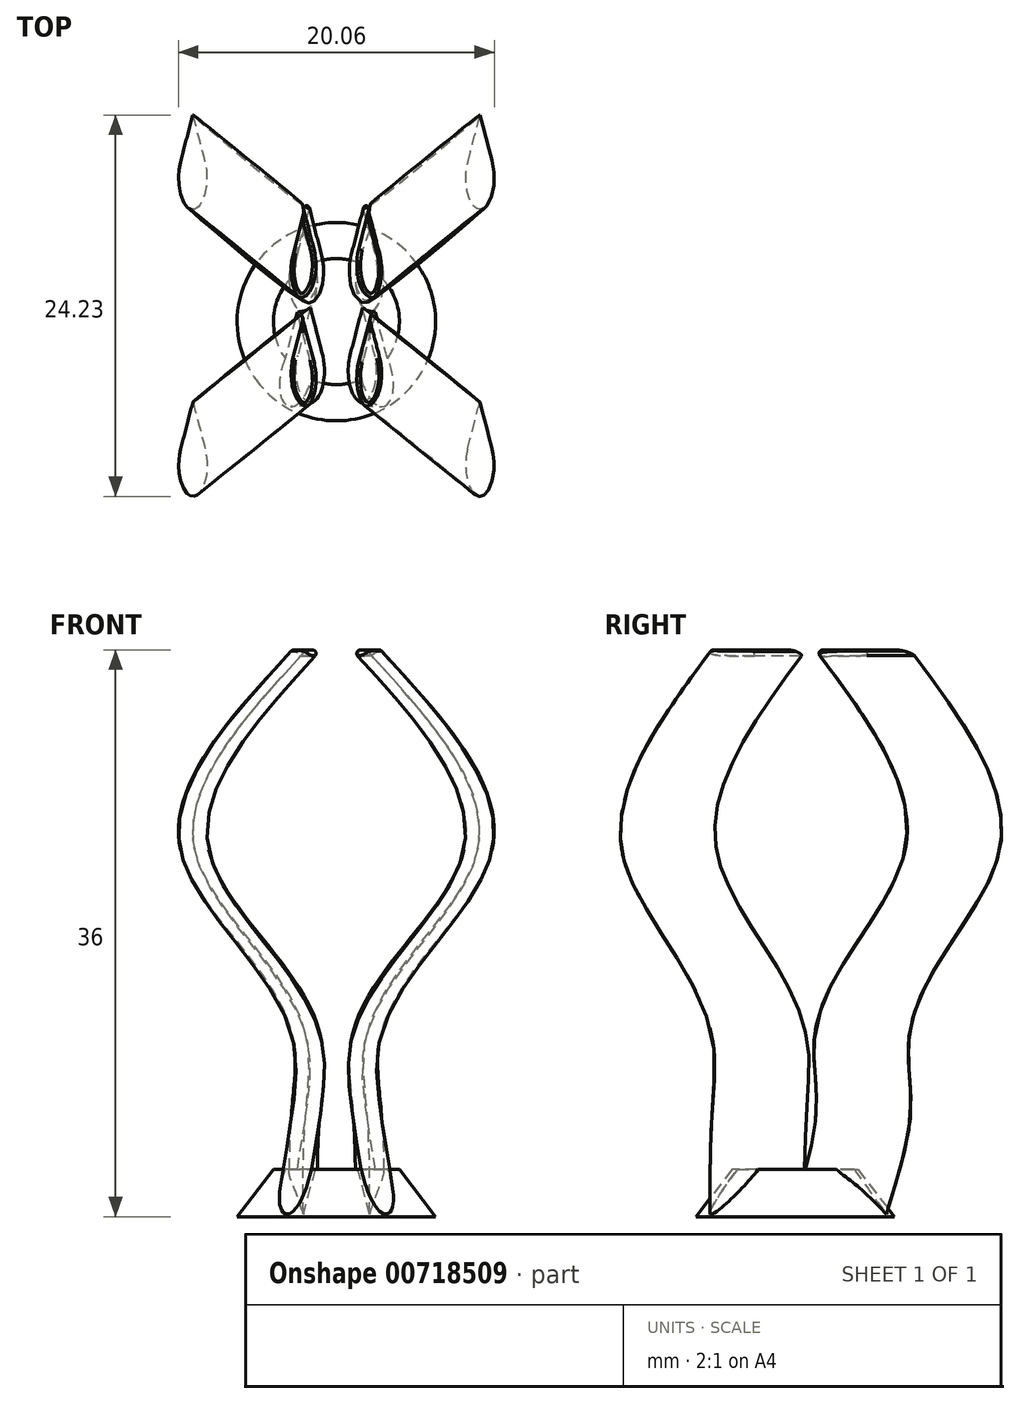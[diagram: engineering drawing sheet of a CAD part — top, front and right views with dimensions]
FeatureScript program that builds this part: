
annotation { "Feature Type Name" : "Feature", "Feature Type Description" : "" }
export const myFeature = defineFeature(function(context is Context, id is Id, definition is map)
    precondition{}
    {
        {
            var Q0;
            Q0=qCreatedBy(makeId("Top.planeOp"),FACE);
            var sketch = newSketch(context, id + "F0", { "sketchPlane" : qUnion([Q0])});
            skCircle(sketch, "E0", {"center": v(0, 0) * mm, "radius": 6.3 * mm});
            skSolve(sketch);
        }
        {
            assignVariable(context, id + "F1", {"variableType" : VariableType.LENGTH, "name" : "BaseHeight", "lengthValue" : 3 * mm});
        }
        {
            var Q0;
            Q0=qCreatedBy(makeId("Top.planeOp"),FACE);
            cPlane(context, id + "F2", {"entities" : qUnion([Q0]), "cplaneType" : CPlaneType.OFFSET, "offset" : getVariable(context, 'BaseHeight'), "width" : 150 * mm, "height" : 150 * mm});
        }
        {
            var Q0;
            Q0=qCreatedBy(id+"F2.planeOp",FACE);
            var sketch = newSketch(context, id + "F3", { "sketchPlane" : qUnion([Q0])});
            skCircle(sketch, "E1", {"center": v(0, 0) * mm, "radius": 4 * mm});
            skSolve(sketch);
        }
        {
            assignVariable(context, id + "F4", {"variableType" : VariableType.LENGTH, "name" : "PostH1", "lengthValue" : 6 * mm});
        }
        {
            assignVariable(context, id + "F5", {"variableType" : VariableType.LENGTH, "name" : "PostH2", "lengthValue" : 11 * mm});
        }
        {
            assignVariable(context, id + "F6", {"variableType" : VariableType.LENGTH, "name" : "PostH3", "lengthValue" : 23.3 * mm});
        }
        {
            assignVariable(context, id + "F7", {"variableType" : VariableType.LENGTH, "name" : "PostH4", "lengthValue" : 36 * mm});
        }
        {
            var Q0;
            Q0=qCreatedBy(makeId("Top.planeOp"),FACE);
            cPlane(context, id + "F8", {"entities" : qUnion([Q0]), "cplaneType" : CPlaneType.OFFSET, "offset" : getVariable(context, 'PostH1'), "width" : 150 * mm, "height" : 150 * mm});
        }
        {
            var Q0;
            Q0=qCreatedBy(makeId("Top.planeOp"),FACE);
            cPlane(context, id + "F9", {"entities" : qUnion([Q0]), "cplaneType" : CPlaneType.OFFSET, "offset" : getVariable(context, 'PostH2'), "width" : 150 * mm, "height" : 150 * mm});
        }
        {
            var Q0;
            Q0=qCreatedBy(makeId("Top.planeOp"),FACE);
            cPlane(context, id + "F10", {"entities" : qUnion([Q0]), "cplaneType" : CPlaneType.OFFSET, "offset" : getVariable(context, 'PostH3'), "width" : 150 * mm, "height" : 150 * mm});
        }
        {
            var Q0;
            Q0=qCreatedBy(makeId("Top.planeOp"),FACE);
            cPlane(context, id + "F11", {"entities" : qUnion([Q0]), "cplaneType" : CPlaneType.OFFSET, "offset" : getVariable(context, 'PostH4'), "width" : 150 * mm, "height" : 150 * mm});
        }
        {
            var Q0;
            Q0=makeQuery(id+"F0.imprint","IMPRINT",FACE,{"disambiguationData":[TD([[makeQuery(id+"F0.imprint","IMPRINT",EDGE,{"derivedFrom":sQuery(id+"F0.wireOp",EDGE,"E0")}),1.0]])]});
            var Q1;
            Q1=makeQuery(id+"F3.imprint","IMPRINT",FACE,{"disambiguationData":[TD([[makeQuery(id+"F3.imprint","IMPRINT",EDGE,{"derivedFrom":sQuery(id+"F3.wireOp",EDGE,"E1")}),1.0]])]});
            loft(context, id + "F12", {"sheetProfilesArray" : [{ "sheetProfileEntities" : qUnion([Q0]) }, { "sheetProfileEntities" : qUnion([Q1]) }]});
        }
        {
            var Q0;
            Q0=qCreatedBy(makeId("Top.planeOp"),FACE);
            var sketch = newSketch(context, id + "F13", { "sketchPlane" : qUnion([Q0])});
            skEllipse(sketch, "E2", {"center": v(-2.1, 1.8) * mm, "majorRadius": 2 * mm, "minorRadius": 0.9 * mm, "majorAxis": v(0, 1)});
            skLineSegment(sketch, "E3", {"start": v(-2.88, 2.8) * mm, "end": v(-2.1, 5.8) * mm});
            skLineSegment(sketch, "E4", {"start": v(-2.1, 5.8) * mm, "end": v(-1.32, 2.8) * mm});
            skEllipse(sketch, "E5", {"center": v(2.1, 1.8) * mm, "majorRadius": 2 * mm, "minorRadius": 0.9 * mm, "majorAxis": v(0, 1)});
            skLineSegment(sketch, "E6", {"start": v(1.32, 2.8) * mm, "end": v(2.1, 5.8) * mm});
            skLineSegment(sketch, "E7", {"start": v(2.1, 5.8) * mm, "end": v(2.88, 2.8) * mm});
            skEllipse(sketch, "E8", {"center": v(-2.9, -3.4) * mm, "majorRadius": 2 * mm, "minorRadius": 0.9 * mm, "majorAxis": v(0, 1)});
            skLineSegment(sketch, "E9", {"start": v(-3.68, -2.4) * mm, "end": v(-2.9, 0.6) * mm});
            skLineSegment(sketch, "E10", {"start": v(-2.9, 0.6) * mm, "end": v(-2.12, -2.4) * mm});
            skEllipse(sketch, "E11", {"center": v(2.9, -3.4) * mm, "majorRadius": 2 * mm, "minorRadius": 0.9 * mm, "majorAxis": v(0, 1)});
            skLineSegment(sketch, "E12", {"start": v(2.12, -2.4) * mm, "end": v(2.9, 0.6) * mm});
            skLineSegment(sketch, "E13", {"start": v(2.9, 0.6) * mm, "end": v(3.68, -2.4) * mm});
            skSolve(sketch);
        }
        {
            var Q0;
            Q0=qCreatedBy(id+"F8.planeOp",FACE);
            var sketch = newSketch(context, id + "F14", { "sketchPlane" : qUnion([Q0])});
            skEllipse(sketch, "E14", {"center": v(-2, 3.3) * mm, "majorRadius": 2 * mm, "minorRadius": 0.9 * mm, "majorAxis": v(0, 1)});
            skLineSegment(sketch, "E15", {"start": v(-2.78, 4.3) * mm, "end": v(-2, 7.3) * mm});
            skLineSegment(sketch, "E16", {"start": v(-2, 7.3) * mm, "end": v(-1.22, 4.3) * mm});
            skEllipse(sketch, "E17", {"center": v(2, 3.3) * mm, "majorRadius": 2 * mm, "minorRadius": 0.9 * mm, "majorAxis": v(0, 1)});
            skLineSegment(sketch, "E18", {"start": v(1.22, 4.3) * mm, "end": v(2, 7.3) * mm});
            skLineSegment(sketch, "E19", {"start": v(2, 7.3) * mm, "end": v(2.78, 4.3) * mm});
            skEllipse(sketch, "E20", {"center": v(-2, -3.3) * mm, "majorRadius": 2 * mm, "minorRadius": 0.9 * mm, "majorAxis": v(0, 1)});
            skLineSegment(sketch, "E21", {"start": v(-2.78, -2.3) * mm, "end": v(-2, 0.7) * mm});
            skLineSegment(sketch, "E22", {"start": v(-2, 0.7) * mm, "end": v(-1.22, -2.3) * mm});
            skEllipse(sketch, "E23", {"center": v(2, -3.3) * mm, "majorRadius": 2 * mm, "minorRadius": 0.9 * mm, "majorAxis": v(0, 1)});
            skLineSegment(sketch, "E24", {"start": v(1.22, -2.3) * mm, "end": v(2, 0.7) * mm});
            skLineSegment(sketch, "E25", {"start": v(2, 0.7) * mm, "end": v(2.78, -2.3) * mm});
            skSolve(sketch);
        }
        {
            var Q0;
            Q0=qCreatedBy(id+"F9.planeOp",FACE);
            var sketch = newSketch(context, id + "F15", { "sketchPlane" : qUnion([Q0])});
            skEllipse(sketch, "E26", {"center": v(-1.8, 3.2) * mm, "majorRadius": 2 * mm, "minorRadius": 0.9 * mm, "majorAxis": v(0, 1)});
            skLineSegment(sketch, "E27", {"start": v(-2.58, 4.2) * mm, "end": v(-1.8, 7.2) * mm});
            skLineSegment(sketch, "E28", {"start": v(-1.8, 7.2) * mm, "end": v(-1.02, 4.2) * mm});
            skEllipse(sketch, "E29", {"center": v(1.8, 3.2) * mm, "majorRadius": 2 * mm, "minorRadius": 0.9 * mm, "majorAxis": v(0, 1)});
            skLineSegment(sketch, "E30", {"start": v(1.02, 4.2) * mm, "end": v(1.8, 7.2) * mm});
            skLineSegment(sketch, "E31", {"start": v(1.8, 7.2) * mm, "end": v(2.58, 4.2) * mm});
            skEllipse(sketch, "E32", {"center": v(-1.8, -3.2) * mm, "majorRadius": 2 * mm, "minorRadius": 0.9 * mm, "majorAxis": v(0, 1)});
            skLineSegment(sketch, "E33", {"start": v(-2.58, -2.2) * mm, "end": v(-1.8, 0.8) * mm});
            skLineSegment(sketch, "E34", {"start": v(-1.8, 0.8) * mm, "end": v(-1.02, -2.2) * mm});
            skEllipse(sketch, "E35", {"center": v(1.8, -3.2) * mm, "majorRadius": 2 * mm, "minorRadius": 0.9 * mm, "majorAxis": v(0, 1)});
            skLineSegment(sketch, "E36", {"start": v(1.02, -2.2) * mm, "end": v(1.8, 0.8) * mm});
            skLineSegment(sketch, "E37", {"start": v(1.8, 0.8) * mm, "end": v(2.58, -2.2) * mm});
            skSolve(sketch);
        }
        {
            var Q0;
            Q0=qCreatedBy(id+"F10.planeOp",FACE);
            var sketch = newSketch(context, id + "F16", { "sketchPlane" : qUnion([Q0])});
            skEllipse(sketch, "E38", {"center": v(-9, 9) * mm, "majorRadius": 2 * mm, "minorRadius": 0.9 * mm, "majorAxis": v(0, 1)});
            skLineSegment(sketch, "E39", {"start": v(-9.78, 10) * mm, "end": v(-9, 13) * mm});
            skLineSegment(sketch, "E40", {"start": v(-9, 13) * mm, "end": v(-8.22, 10) * mm});
            skEllipse(sketch, "E41", {"center": v(9, 9) * mm, "majorRadius": 2 * mm, "minorRadius": 0.9 * mm, "majorAxis": v(0, 1)});
            skLineSegment(sketch, "E42", {"start": v(8.22, 10) * mm, "end": v(9, 13) * mm});
            skLineSegment(sketch, "E43", {"start": v(9, 13) * mm, "end": v(9.78, 10) * mm});
            skEllipse(sketch, "E44", {"center": v(-9, -9) * mm, "majorRadius": 2 * mm, "minorRadius": 0.9 * mm, "majorAxis": v(0, 1)});
            skLineSegment(sketch, "E45", {"start": v(-9.78, -8) * mm, "end": v(-9, -5) * mm});
            skLineSegment(sketch, "E46", {"start": v(-9, -5) * mm, "end": v(-8.22, -8) * mm});
            skEllipse(sketch, "E47", {"center": v(9, -9) * mm, "majorRadius": 2 * mm, "minorRadius": 0.9 * mm, "majorAxis": v(0, 1)});
            skLineSegment(sketch, "E48", {"start": v(8.22, -8) * mm, "end": v(9, -5) * mm});
            skLineSegment(sketch, "E49", {"start": v(9, -5) * mm, "end": v(9.78, -8) * mm});
            skSolve(sketch);
        }
        {
            var Q0;
            Q0=qCreatedBy(id+"F11.planeOp",FACE);
            var sketch = newSketch(context, id + "F17", { "sketchPlane" : qUnion([Q0])});
            skEllipse(sketch, "E50", {"center": v(-1.9, 3.3) * mm, "majorRadius": 2 * mm, "minorRadius": 0.9 * mm, "majorAxis": v(0, 1)});
            skLineSegment(sketch, "E51", {"start": v(-2.68, 4.3) * mm, "end": v(-1.9, 7.3) * mm});
            skLineSegment(sketch, "E52", {"start": v(-1.9, 7.3) * mm, "end": v(-1.12, 4.3) * mm});
            skEllipse(sketch, "E53", {"center": v(1.9, 3.3) * mm, "majorRadius": 2 * mm, "minorRadius": 0.9 * mm, "majorAxis": v(0, 1)});
            skLineSegment(sketch, "E54", {"start": v(1.12, 4.3) * mm, "end": v(1.9, 7.3) * mm});
            skLineSegment(sketch, "E55", {"start": v(1.9, 7.3) * mm, "end": v(2.68, 4.3) * mm});
            skEllipse(sketch, "E56", {"center": v(-1.9, -3.3) * mm, "majorRadius": 2 * mm, "minorRadius": 0.9 * mm, "majorAxis": v(0, 1)});
            skLineSegment(sketch, "E57", {"start": v(-2.68, -2.3) * mm, "end": v(-1.9, 0.7) * mm});
            skLineSegment(sketch, "E58", {"start": v(-1.9, 0.7) * mm, "end": v(-1.12, -2.3) * mm});
            skEllipse(sketch, "E59", {"center": v(1.9, -3.3) * mm, "majorRadius": 2 * mm, "minorRadius": 0.9 * mm, "majorAxis": v(0, 1)});
            skLineSegment(sketch, "E60", {"start": v(1.12, -2.3) * mm, "end": v(1.9, 0.7) * mm});
            skLineSegment(sketch, "E61", {"start": v(1.9, 0.7) * mm, "end": v(2.68, -2.3) * mm});
            skSolve(sketch);
        }
        {
            assignVariable(context, id + "F18", {"variableType" : VariableType.NUMBER, "name" : "Loft1", "numberValue" : 0.3});
        }
        {
            var Q0;
            {var subQ0=sQuery(id+"F13.wireOp",EDGE,"E5");var subQ1=makeQuery(id+"F13.imprint","INTERSECT",VERTEX,{"derivedFrom":[subQ0,sQuery(id+"F13.wireOp",EDGE,"E6")]});Q0=makeQuery(id+"F13.imprint","IMPRINT",FACE,{"disambiguationData":[TD([[makeQuery(id+"F13.imprint","IMPRINT",EDGE,{"disambiguationData":[TD([[subQ1,-1.0]])],"derivedFrom":subQ0}),1.0]])]});}
            var Q1;
            {var subQ0=sQuery(id+"F13.wireOp",EDGE,"E6");Q1=makeQuery(id+"F13.imprint","IMPRINT",FACE,{"disambiguationData":[TD([[makeQuery(id+"F13.imprint","IMPRINT",EDGE,{"derivedFrom":subQ0}),-1.0]])]});}
            var Q2;
            {var subQ0=sQuery(id+"F14.wireOp",EDGE,"E17");var subQ1=makeQuery(id+"F14.imprint","INTERSECT",VERTEX,{"derivedFrom":[subQ0,sQuery(id+"F14.wireOp",EDGE,"E18")]});Q2=makeQuery(id+"F14.imprint","IMPRINT",FACE,{"disambiguationData":[TD([[makeQuery(id+"F14.imprint","IMPRINT",EDGE,{"disambiguationData":[TD([[subQ1,-1.0]])],"derivedFrom":subQ0}),1.0]])]});}
            var Q3;
            {var subQ0=sQuery(id+"F14.wireOp",EDGE,"E18");Q3=makeQuery(id+"F14.imprint","IMPRINT",FACE,{"disambiguationData":[TD([[makeQuery(id+"F14.imprint","IMPRINT",EDGE,{"derivedFrom":subQ0}),-1.0]])]});}
            var Q4;
            {var subQ0=sQuery(id+"F15.wireOp",EDGE,"E29");var subQ1=makeQuery(id+"F15.imprint","INTERSECT",VERTEX,{"derivedFrom":[subQ0,sQuery(id+"F15.wireOp",EDGE,"E30")]});Q4=makeQuery(id+"F15.imprint","IMPRINT",FACE,{"disambiguationData":[TD([[makeQuery(id+"F15.imprint","IMPRINT",EDGE,{"disambiguationData":[TD([[subQ1,-1.0]])],"derivedFrom":subQ0}),1.0]])]});}
            var Q5;
            {var subQ0=sQuery(id+"F15.wireOp",EDGE,"E30");Q5=makeQuery(id+"F15.imprint","IMPRINT",FACE,{"disambiguationData":[TD([[makeQuery(id+"F15.imprint","IMPRINT",EDGE,{"derivedFrom":subQ0}),-1.0]])]});}
            var Q6;
            {var subQ0=sQuery(id+"F16.wireOp",EDGE,"E41");var subQ1=makeQuery(id+"F16.imprint","INTERSECT",VERTEX,{"derivedFrom":[subQ0,sQuery(id+"F16.wireOp",EDGE,"E42")]});Q6=makeQuery(id+"F16.imprint","IMPRINT",FACE,{"disambiguationData":[TD([[makeQuery(id+"F16.imprint","IMPRINT",EDGE,{"disambiguationData":[TD([[subQ1,-1.0]])],"derivedFrom":subQ0}),1.0]])]});}
            var Q7;
            {var subQ0=sQuery(id+"F16.wireOp",EDGE,"E42");Q7=makeQuery(id+"F16.imprint","IMPRINT",FACE,{"disambiguationData":[TD([[makeQuery(id+"F16.imprint","IMPRINT",EDGE,{"derivedFrom":subQ0}),-1.0]])]});}
            var Q8;
            {var subQ0=sQuery(id+"F17.wireOp",EDGE,"E53");var subQ1=makeQuery(id+"F17.imprint","INTERSECT",VERTEX,{"derivedFrom":[subQ0,sQuery(id+"F17.wireOp",EDGE,"E54")]});Q8=makeQuery(id+"F17.imprint","IMPRINT",FACE,{"disambiguationData":[TD([[makeQuery(id+"F17.imprint","IMPRINT",EDGE,{"disambiguationData":[TD([[subQ1,-1.0]])],"derivedFrom":subQ0}),1.0]])]});}
            var Q9;
            {var subQ0=sQuery(id+"F17.wireOp",EDGE,"E54");Q9=makeQuery(id+"F17.imprint","IMPRINT",FACE,{"disambiguationData":[TD([[makeQuery(id+"F17.imprint","IMPRINT",EDGE,{"derivedFrom":subQ0}),-1.0]])]});}
            loft(context, id + "F19", {"operationType" : NewBodyOperationType.ADD, "sheetProfilesArray" : [{ "sheetProfileEntities" : qUnion([Q0, Q1]) }, { "sheetProfileEntities" : qUnion([Q2, Q3]) }, { "sheetProfileEntities" : qUnion([Q4, Q5]) }, { "sheetProfileEntities" : qUnion([Q6, Q7]) }, { "sheetProfileEntities" : qUnion([Q8, Q9]) }], "startCondition" : LoftEndDerivativeType.NORMAL_TO_PROFILE, "startMagnitude" : getVariable(context, 'Loft1')});
        }
        {
            var Q0;
            {var subQ0=sQuery(id+"F13.wireOp",EDGE,"E3");Q0=makeQuery(id+"F13.imprint","IMPRINT",FACE,{"disambiguationData":[TD([[makeQuery(id+"F13.imprint","IMPRINT",EDGE,{"derivedFrom":subQ0}),-1.0]])]});}
            var Q1;
            {var subQ0=sQuery(id+"F13.wireOp",EDGE,"E2");var subQ1=makeQuery(id+"F13.imprint","INTERSECT",VERTEX,{"derivedFrom":[subQ0,sQuery(id+"F13.wireOp",EDGE,"E3")]});Q1=makeQuery(id+"F13.imprint","IMPRINT",FACE,{"disambiguationData":[TD([[makeQuery(id+"F13.imprint","IMPRINT",EDGE,{"disambiguationData":[TD([[subQ1,-1.0]])],"derivedFrom":subQ0}),1.0]])]});}
            var Q2;
            {var subQ0=sQuery(id+"F14.wireOp",EDGE,"E15");Q2=makeQuery(id+"F14.imprint","IMPRINT",FACE,{"disambiguationData":[TD([[makeQuery(id+"F14.imprint","IMPRINT",EDGE,{"derivedFrom":subQ0}),-1.0]])]});}
            var Q3;
            {var subQ0=sQuery(id+"F14.wireOp",EDGE,"E14");var subQ1=makeQuery(id+"F14.imprint","INTERSECT",VERTEX,{"derivedFrom":[subQ0,sQuery(id+"F14.wireOp",EDGE,"E15")]});Q3=makeQuery(id+"F14.imprint","IMPRINT",FACE,{"disambiguationData":[TD([[makeQuery(id+"F14.imprint","IMPRINT",EDGE,{"disambiguationData":[TD([[subQ1,-1.0]])],"derivedFrom":subQ0}),1.0]])]});}
            var Q4;
            {var subQ0=sQuery(id+"F15.wireOp",EDGE,"E26");var subQ1=makeQuery(id+"F15.imprint","INTERSECT",VERTEX,{"derivedFrom":[subQ0,sQuery(id+"F15.wireOp",EDGE,"E27")]});Q4=makeQuery(id+"F15.imprint","IMPRINT",FACE,{"disambiguationData":[TD([[makeQuery(id+"F15.imprint","IMPRINT",EDGE,{"disambiguationData":[TD([[subQ1,-1.0]])],"derivedFrom":subQ0}),1.0]])]});}
            var Q5;
            {var subQ0=sQuery(id+"F15.wireOp",EDGE,"E27");Q5=makeQuery(id+"F15.imprint","IMPRINT",FACE,{"disambiguationData":[TD([[makeQuery(id+"F15.imprint","IMPRINT",EDGE,{"derivedFrom":subQ0}),-1.0]])]});}
            var Q6;
            {var subQ0=sQuery(id+"F16.wireOp",EDGE,"E38");var subQ1=makeQuery(id+"F16.imprint","INTERSECT",VERTEX,{"derivedFrom":[subQ0,sQuery(id+"F16.wireOp",EDGE,"E39")]});Q6=makeQuery(id+"F16.imprint","IMPRINT",FACE,{"disambiguationData":[TD([[makeQuery(id+"F16.imprint","IMPRINT",EDGE,{"disambiguationData":[TD([[subQ1,-1.0]])],"derivedFrom":subQ0}),1.0]])]});}
            var Q7;
            {var subQ0=sQuery(id+"F16.wireOp",EDGE,"E39");Q7=makeQuery(id+"F16.imprint","IMPRINT",FACE,{"disambiguationData":[TD([[makeQuery(id+"F16.imprint","IMPRINT",EDGE,{"derivedFrom":subQ0}),-1.0]])]});}
            var Q8;
            {var subQ0=sQuery(id+"F17.wireOp",EDGE,"E50");var subQ1=makeQuery(id+"F17.imprint","INTERSECT",VERTEX,{"derivedFrom":[subQ0,sQuery(id+"F17.wireOp",EDGE,"E51")]});Q8=makeQuery(id+"F17.imprint","IMPRINT",FACE,{"disambiguationData":[TD([[makeQuery(id+"F17.imprint","IMPRINT",EDGE,{"disambiguationData":[TD([[subQ1,-1.0]])],"derivedFrom":subQ0}),1.0]])]});}
            var Q9;
            {var subQ0=sQuery(id+"F17.wireOp",EDGE,"E51");Q9=makeQuery(id+"F17.imprint","IMPRINT",FACE,{"disambiguationData":[TD([[makeQuery(id+"F17.imprint","IMPRINT",EDGE,{"derivedFrom":subQ0}),-1.0]])]});}
            loft(context, id + "F20", {"operationType" : NewBodyOperationType.ADD, "sheetProfilesArray" : [{ "sheetProfileEntities" : qUnion([Q0, Q1]) }, { "sheetProfileEntities" : qUnion([Q2, Q3]) }, { "sheetProfileEntities" : qUnion([Q4, Q5]) }, { "sheetProfileEntities" : qUnion([Q6, Q7]) }, { "sheetProfileEntities" : qUnion([Q8, Q9]) }], "startCondition" : LoftEndDerivativeType.NORMAL_TO_PROFILE, "startMagnitude" : getVariable(context, 'Loft1')});
        }
        {
            var Q0;
            {var subQ0=sQuery(id+"F13.wireOp",EDGE,"E9");Q0=makeQuery(id+"F13.imprint","IMPRINT",FACE,{"disambiguationData":[TD([[makeQuery(id+"F13.imprint","IMPRINT",EDGE,{"derivedFrom":subQ0}),-1.0]])]});}
            var Q1;
            {var subQ0=sQuery(id+"F13.wireOp",EDGE,"E8");var subQ1=makeQuery(id+"F13.imprint","INTERSECT",VERTEX,{"derivedFrom":[subQ0,sQuery(id+"F13.wireOp",EDGE,"E9")]});Q1=makeQuery(id+"F13.imprint","IMPRINT",FACE,{"disambiguationData":[TD([[makeQuery(id+"F13.imprint","IMPRINT",EDGE,{"disambiguationData":[TD([[subQ1,-1.0]])],"derivedFrom":subQ0}),1.0]])]});}
            var Q2;
            {var subQ0=sQuery(id+"F14.wireOp",EDGE,"E21");Q2=makeQuery(id+"F14.imprint","IMPRINT",FACE,{"disambiguationData":[TD([[makeQuery(id+"F14.imprint","IMPRINT",EDGE,{"derivedFrom":subQ0}),-1.0]])]});}
            var Q3;
            {var subQ0=sQuery(id+"F14.wireOp",EDGE,"E20");var subQ1=makeQuery(id+"F14.imprint","INTERSECT",VERTEX,{"derivedFrom":[subQ0,sQuery(id+"F14.wireOp",EDGE,"E21")]});Q3=makeQuery(id+"F14.imprint","IMPRINT",FACE,{"disambiguationData":[TD([[makeQuery(id+"F14.imprint","IMPRINT",EDGE,{"disambiguationData":[TD([[subQ1,-1.0]])],"derivedFrom":subQ0}),1.0]])]});}
            var Q4;
            {var subQ0=sQuery(id+"F15.wireOp",EDGE,"E32");var subQ1=makeQuery(id+"F15.imprint","INTERSECT",VERTEX,{"derivedFrom":[subQ0,sQuery(id+"F15.wireOp",EDGE,"E33")]});Q4=makeQuery(id+"F15.imprint","IMPRINT",FACE,{"disambiguationData":[TD([[makeQuery(id+"F15.imprint","IMPRINT",EDGE,{"disambiguationData":[TD([[subQ1,-1.0]])],"derivedFrom":subQ0}),1.0]])]});}
            var Q5;
            {var subQ0=sQuery(id+"F15.wireOp",EDGE,"E33");Q5=makeQuery(id+"F15.imprint","IMPRINT",FACE,{"disambiguationData":[TD([[makeQuery(id+"F15.imprint","IMPRINT",EDGE,{"derivedFrom":subQ0}),-1.0]])]});}
            var Q6;
            {var subQ0=sQuery(id+"F16.wireOp",EDGE,"E44");var subQ1=makeQuery(id+"F16.imprint","INTERSECT",VERTEX,{"derivedFrom":[subQ0,sQuery(id+"F16.wireOp",EDGE,"E45")]});Q6=makeQuery(id+"F16.imprint","IMPRINT",FACE,{"disambiguationData":[TD([[makeQuery(id+"F16.imprint","IMPRINT",EDGE,{"disambiguationData":[TD([[subQ1,-1.0]])],"derivedFrom":subQ0}),1.0]])]});}
            var Q7;
            {var subQ0=sQuery(id+"F16.wireOp",EDGE,"E45");Q7=makeQuery(id+"F16.imprint","IMPRINT",FACE,{"disambiguationData":[TD([[makeQuery(id+"F16.imprint","IMPRINT",EDGE,{"derivedFrom":subQ0}),-1.0]])]});}
            var Q8;
            {var subQ0=sQuery(id+"F17.wireOp",EDGE,"E56");var subQ1=makeQuery(id+"F17.imprint","INTERSECT",VERTEX,{"derivedFrom":[subQ0,sQuery(id+"F17.wireOp",EDGE,"E57")]});Q8=makeQuery(id+"F17.imprint","IMPRINT",FACE,{"disambiguationData":[TD([[makeQuery(id+"F17.imprint","IMPRINT",EDGE,{"disambiguationData":[TD([[subQ1,-1.0]])],"derivedFrom":subQ0}),1.0]])]});}
            var Q9;
            {var subQ0=sQuery(id+"F17.wireOp",EDGE,"E57");Q9=makeQuery(id+"F17.imprint","IMPRINT",FACE,{"disambiguationData":[TD([[makeQuery(id+"F17.imprint","IMPRINT",EDGE,{"derivedFrom":subQ0}),-1.0]])]});}
            loft(context, id + "F21", {"operationType" : NewBodyOperationType.ADD, "sheetProfilesArray" : [{ "sheetProfileEntities" : qUnion([Q0, Q1]) }, { "sheetProfileEntities" : qUnion([Q2, Q3]) }, { "sheetProfileEntities" : qUnion([Q4, Q5]) }, { "sheetProfileEntities" : qUnion([Q6, Q7]) }, { "sheetProfileEntities" : qUnion([Q8, Q9]) }], "startCondition" : LoftEndDerivativeType.NORMAL_TO_PROFILE, "startMagnitude" : getVariable(context, 'Loft1')});
        }
        {
            var Q0;
            {var subQ0=sQuery(id+"F13.wireOp",EDGE,"E11");var subQ1=makeQuery(id+"F13.imprint","INTERSECT",VERTEX,{"derivedFrom":[subQ0,sQuery(id+"F13.wireOp",EDGE,"E12")]});Q0=makeQuery(id+"F13.imprint","IMPRINT",FACE,{"disambiguationData":[TD([[makeQuery(id+"F13.imprint","IMPRINT",EDGE,{"disambiguationData":[TD([[subQ1,-1.0]])],"derivedFrom":subQ0}),1.0]])]});}
            var Q1;
            {var subQ0=sQuery(id+"F13.wireOp",EDGE,"E12");Q1=makeQuery(id+"F13.imprint","IMPRINT",FACE,{"disambiguationData":[TD([[makeQuery(id+"F13.imprint","IMPRINT",EDGE,{"derivedFrom":subQ0}),-1.0]])]});}
            var Q2;
            {var subQ0=sQuery(id+"F14.wireOp",EDGE,"E23");var subQ1=makeQuery(id+"F14.imprint","INTERSECT",VERTEX,{"derivedFrom":[subQ0,sQuery(id+"F14.wireOp",EDGE,"E24")]});Q2=makeQuery(id+"F14.imprint","IMPRINT",FACE,{"disambiguationData":[TD([[makeQuery(id+"F14.imprint","IMPRINT",EDGE,{"disambiguationData":[TD([[subQ1,-1.0]])],"derivedFrom":subQ0}),1.0]])]});}
            var Q3;
            {var subQ0=sQuery(id+"F14.wireOp",EDGE,"E24");Q3=makeQuery(id+"F14.imprint","IMPRINT",FACE,{"disambiguationData":[TD([[makeQuery(id+"F14.imprint","IMPRINT",EDGE,{"derivedFrom":subQ0}),-1.0]])]});}
            var Q4;
            {var subQ0=sQuery(id+"F15.wireOp",EDGE,"E35");var subQ1=makeQuery(id+"F15.imprint","INTERSECT",VERTEX,{"derivedFrom":[subQ0,sQuery(id+"F15.wireOp",EDGE,"E36")]});Q4=makeQuery(id+"F15.imprint","IMPRINT",FACE,{"disambiguationData":[TD([[makeQuery(id+"F15.imprint","IMPRINT",EDGE,{"disambiguationData":[TD([[subQ1,-1.0]])],"derivedFrom":subQ0}),1.0]])]});}
            var Q5;
            {var subQ0=sQuery(id+"F15.wireOp",EDGE,"E36");Q5=makeQuery(id+"F15.imprint","IMPRINT",FACE,{"disambiguationData":[TD([[makeQuery(id+"F15.imprint","IMPRINT",EDGE,{"derivedFrom":subQ0}),-1.0]])]});}
            var Q6;
            {var subQ0=sQuery(id+"F16.wireOp",EDGE,"E47");var subQ1=makeQuery(id+"F16.imprint","INTERSECT",VERTEX,{"derivedFrom":[subQ0,sQuery(id+"F16.wireOp",EDGE,"E48")]});Q6=makeQuery(id+"F16.imprint","IMPRINT",FACE,{"disambiguationData":[TD([[makeQuery(id+"F16.imprint","IMPRINT",EDGE,{"disambiguationData":[TD([[subQ1,-1.0]])],"derivedFrom":subQ0}),1.0]])]});}
            var Q7;
            {var subQ0=sQuery(id+"F16.wireOp",EDGE,"E48");Q7=makeQuery(id+"F16.imprint","IMPRINT",FACE,{"disambiguationData":[TD([[makeQuery(id+"F16.imprint","IMPRINT",EDGE,{"derivedFrom":subQ0}),-1.0]])]});}
            var Q8;
            {var subQ0=sQuery(id+"F17.wireOp",EDGE,"E59");var subQ1=makeQuery(id+"F17.imprint","INTERSECT",VERTEX,{"derivedFrom":[subQ0,sQuery(id+"F17.wireOp",EDGE,"E60")]});Q8=makeQuery(id+"F17.imprint","IMPRINT",FACE,{"disambiguationData":[TD([[makeQuery(id+"F17.imprint","IMPRINT",EDGE,{"disambiguationData":[TD([[subQ1,-1.0]])],"derivedFrom":subQ0}),1.0]])]});}
            var Q9;
            {var subQ0=sQuery(id+"F17.wireOp",EDGE,"E60");Q9=makeQuery(id+"F17.imprint","IMPRINT",FACE,{"disambiguationData":[TD([[makeQuery(id+"F17.imprint","IMPRINT",EDGE,{"derivedFrom":subQ0}),-1.0]])]});}
            loft(context, id + "F22", {"operationType" : NewBodyOperationType.ADD, "sheetProfilesArray" : [{ "sheetProfileEntities" : qUnion([Q0, Q1]) }, { "sheetProfileEntities" : qUnion([Q2, Q3]) }, { "sheetProfileEntities" : qUnion([Q4, Q5]) }, { "sheetProfileEntities" : qUnion([Q6, Q7]) }, { "sheetProfileEntities" : qUnion([Q8, Q9]) }], "startCondition" : LoftEndDerivativeType.NORMAL_TO_PROFILE, "startMagnitude" : getVariable(context, 'Loft1')});
        }
        {
            var Q0;
            {var subQ0=sQuery(id+"F17.wireOp",EDGE,"E57");var subQ1=sQuery(id+"F17.wireOp",EDGE,"E56");var subQ2=makeQuery(id+"F17.imprint","INTERSECT",VERTEX,{"derivedFrom":[subQ1,subQ0]});Q0=makeQuery(id+"F21.opLoft","CAP_FACE",FACE,{"disambiguationData":[OSD([makeQuery(id+"F17.imprint","IMPRINT",FACE,{"disambiguationData":[TD([[makeQuery(id+"F17.imprint","IMPRINT",EDGE,{"disambiguationData":[TD([[subQ2,-1.0]])],"derivedFrom":subQ1}),1.0]])]}),makeQuery(id+"F17.imprint","IMPRINT",FACE,{"disambiguationData":[TD([[makeQuery(id+"F17.imprint","IMPRINT",EDGE,{"derivedFrom":subQ0}),-1.0]])]})])],"isStart":true});}
            var Q1;
            {var subQ0=sQuery(id+"F17.wireOp",EDGE,"E51");var subQ1=sQuery(id+"F17.wireOp",EDGE,"E50");var subQ2=makeQuery(id+"F17.imprint","INTERSECT",VERTEX,{"derivedFrom":[subQ1,subQ0]});Q1=makeQuery(id+"F20.opLoft","CAP_FACE",FACE,{"disambiguationData":[OSD([makeQuery(id+"F17.imprint","IMPRINT",FACE,{"disambiguationData":[TD([[makeQuery(id+"F17.imprint","IMPRINT",EDGE,{"disambiguationData":[TD([[subQ2,-1.0]])],"derivedFrom":subQ1}),1.0]])]}),makeQuery(id+"F17.imprint","IMPRINT",FACE,{"disambiguationData":[TD([[makeQuery(id+"F17.imprint","IMPRINT",EDGE,{"derivedFrom":subQ0}),-1.0]])]})])],"isStart":true});}
            var Q2;
            {var subQ0=sQuery(id+"F17.wireOp",EDGE,"E60");var subQ1=sQuery(id+"F17.wireOp",EDGE,"E59");var subQ2=makeQuery(id+"F17.imprint","INTERSECT",VERTEX,{"derivedFrom":[subQ1,subQ0]});Q2=makeQuery(id+"F22.opLoft","CAP_FACE",FACE,{"disambiguationData":[OSD([makeQuery(id+"F17.imprint","IMPRINT",FACE,{"disambiguationData":[TD([[makeQuery(id+"F17.imprint","IMPRINT",EDGE,{"disambiguationData":[TD([[subQ2,-1.0]])],"derivedFrom":subQ1}),1.0]])]}),makeQuery(id+"F17.imprint","IMPRINT",FACE,{"disambiguationData":[TD([[makeQuery(id+"F17.imprint","IMPRINT",EDGE,{"derivedFrom":subQ0}),-1.0]])]})])],"isStart":true});}
            var Q3;
            {var subQ0=sQuery(id+"F17.wireOp",EDGE,"E54");var subQ1=sQuery(id+"F17.wireOp",EDGE,"E53");var subQ2=makeQuery(id+"F17.imprint","INTERSECT",VERTEX,{"derivedFrom":[subQ1,subQ0]});Q3=makeQuery(id+"F19.opLoft","CAP_FACE",FACE,{"disambiguationData":[OSD([makeQuery(id+"F17.imprint","IMPRINT",FACE,{"disambiguationData":[TD([[makeQuery(id+"F17.imprint","IMPRINT",EDGE,{"disambiguationData":[TD([[subQ2,-1.0]])],"derivedFrom":subQ1}),1.0]])]}),makeQuery(id+"F17.imprint","IMPRINT",FACE,{"disambiguationData":[TD([[makeQuery(id+"F17.imprint","IMPRINT",EDGE,{"derivedFrom":subQ0}),-1.0]])]})])],"isStart":true});}
            var Q4;
            Q4=makeQuery(id+"F21.opLoft","MID_CAP_VERTEX",VERTEX,{"disambiguationData":[OSD([sQuery(id+"F17.wireOp",EDGE,"E57"),sQuery(id+"F17.wireOp",EDGE,"E58")])],"capPos":3.0});
            var Q5;
            Q5=makeQuery(id+"F21.opLoft","MID_CAP_VERTEX",VERTEX,{"disambiguationData":[OSD([sQuery(id+"F17.wireOp",EDGE,"E56"),sQuery(id+"F17.wireOp",EDGE,"E57")])],"capPos":3.0});
            var Q6;
            Q6=makeQuery(id+"F21.opLoft","MID_CAP_VERTEX",VERTEX,{"disambiguationData":[OSD([sQuery(id+"F17.wireOp",EDGE,"E56"),sQuery(id+"F17.wireOp",EDGE,"E58")])],"capPos":3.0});
            fillet(context, id + "F23", {"entities" : qUnion([Q0, Q1, Q2, Q3]), "tangentPropagation" : true, "radius" : 0.23 * mm, "defaultsChanged" : true, "vertexSettings" : [{ "vertex" : qUnion([Q4]), "vertexRadius" : { 'value' : try(0.25 * mm), 'expression' : "0.25 mm" }.value, "variableRho" : { 'value' : try(0.5), 'expression' : "0.5" }.value, "variableMagnitude" : { 'value' : try(0.5), 'expression' : "0.5" }.value }, { "vertex" : qUnion([Q5]), "vertexRadius" : { 'value' : try(0.2 * mm), 'expression' : "0.2 mm" }.value, "variableRho" : { 'value' : try(0.5), 'expression' : "0.5" }.value, "variableMagnitude" : { 'value' : try(0.5), 'expression' : "0.5" }.value }, { "vertex" : qUnion([Q6]), "vertexRadius" : { 'value' : try(0.25 * mm), 'expression' : "0.25 mm" }.value, "variableRho" : { 'value' : try(0.5), 'expression' : "0.5" }.value, "variableMagnitude" : { 'value' : try(0.5), 'expression' : "0.5" }.value }]});
        }
    });
